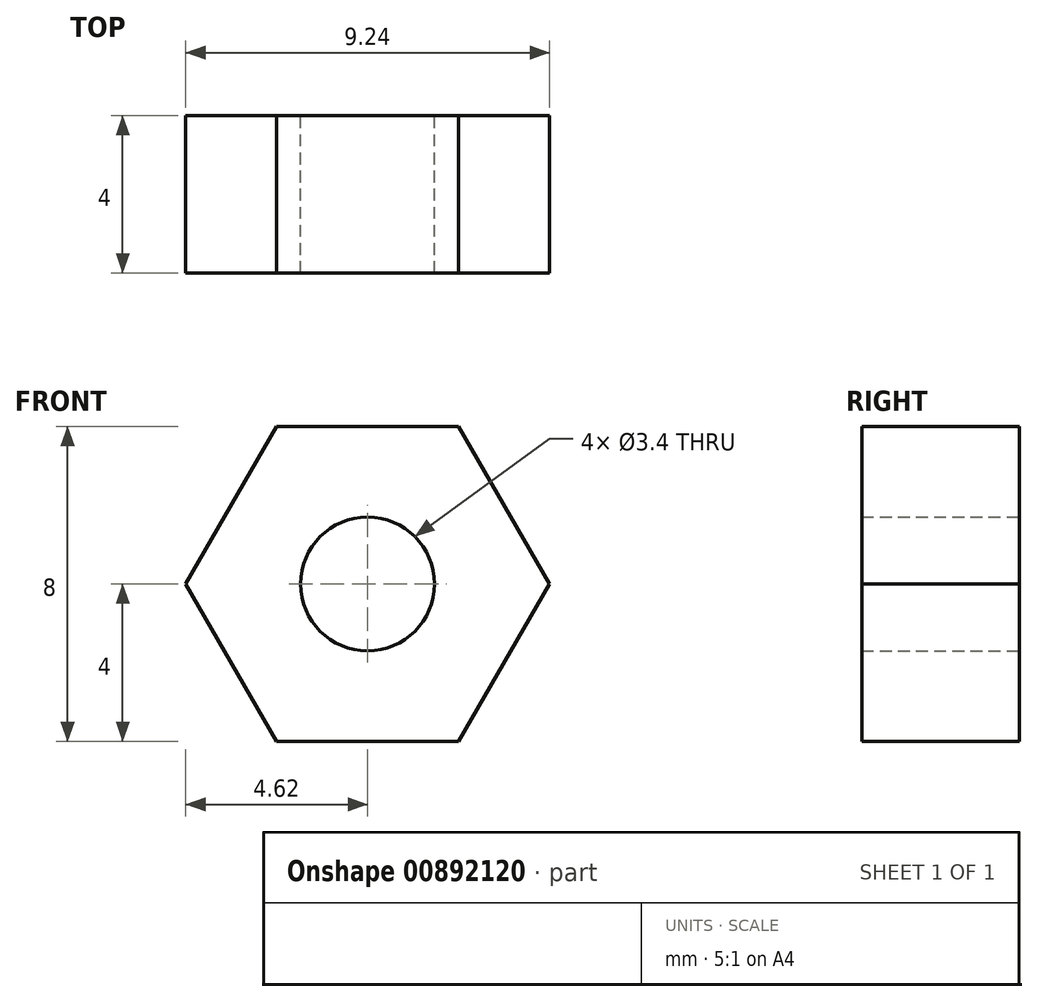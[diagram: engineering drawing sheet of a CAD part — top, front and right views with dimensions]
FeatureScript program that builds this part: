
annotation { "Feature Type Name" : "Feature", "Feature Type Description" : "" }
export const myFeature = defineFeature(function(context is Context, id is Id, definition is map)
    precondition{}
    {
        {
            var Q0;
            Q0=qCreatedBy(makeId("Front.planeOp"),FACE);
            var sketch = newSketch(context, id + "F0", { "sketchPlane" : qUnion([Q0])});
            skCircle(sketch, "E0", {"center": v(0, 4) * mm, "radius": 1.7 * mm});
            skPoint(sketch, "E0.centerSnap0", {"position": v(0, 4) * mm});
            skPoint(sketch, "E0.centerSnap1", {"position": v(0, 0) * mm});
            skPoint(sketch, "E1.orphan", {"position": v(0, 8) * mm});
            skCircle(sketch, "E2.cCircle", {"center": v(0, 4) * mm, "radius": 4 * mm, "construction": true});
            skLineSegment(sketch, "E2.0", {"start": v(-2.3, 8) * mm, "end": v(2.3, 8) * mm});
            skLineSegment(sketch, "E2.1", {"start": v(2.3, 8) * mm, "end": v(4.62, 4) * mm});
            skLineSegment(sketch, "E2.2", {"start": v(4.62, 4) * mm, "end": v(2.3, 0) * mm});
            skLineSegment(sketch, "E2.3", {"start": v(2.3, 0) * mm, "end": v(-2.3, 0) * mm});
            skLineSegment(sketch, "E2.4", {"start": v(-2.3, 0) * mm, "end": v(-4.62, 4) * mm});
            skLineSegment(sketch, "E2.5", {"start": v(-4.62, 4) * mm, "end": v(-2.3, 8) * mm});
            skSolve(sketch);
        }
        {
            var Q0;
            Q0=qSketchRegion(id+"F0",true);
            extrude(context, id + "F1", {"entities" : qUnion([Q0]), "depth" : 4 * mm});
        }
    });
